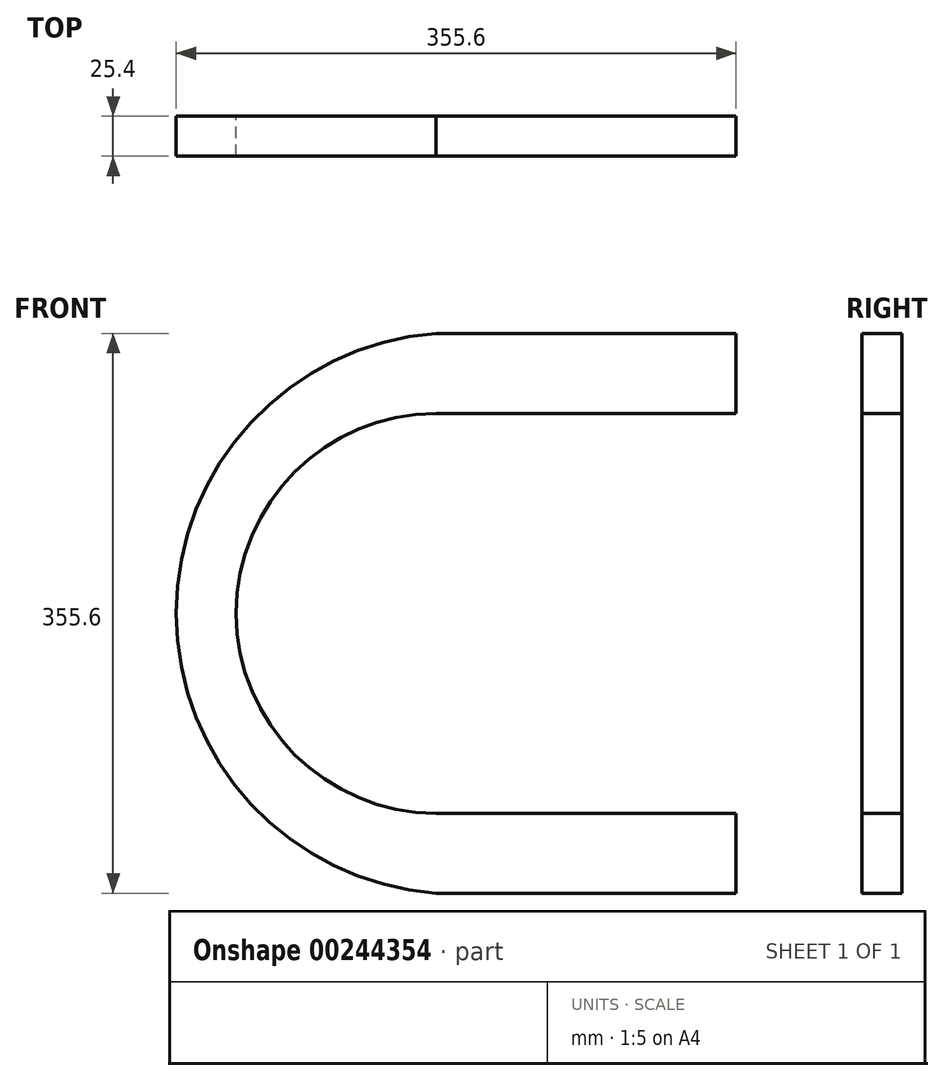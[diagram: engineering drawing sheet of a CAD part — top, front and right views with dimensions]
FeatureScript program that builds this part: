
annotation { "Feature Type Name" : "Feature", "Feature Type Description" : "" }
export const myFeature = defineFeature(function(context is Context, id is Id, definition is map)
    precondition{}
    {
        {
            var Q0;
            Q0=qCreatedBy(makeId("Front.planeOp"),FACE);
            var sketch = newSketch(context, id + "F0", { "sketchPlane" : qUnion([Q0])});
            skLineSegment(sketch, "E0.bottom", {"start": v(190.5, 177.8) * mm, "end": v(-190.5, 177.8) * mm});
            skLineSegment(sketch, "E0.top", {"start": v(190.5, -177.8) * mm, "end": v(-190.5, -177.8) * mm});
            skLineSegment(sketch, "E0.left", {"start": v(190.5, 177.8) * mm, "end": v(190.5, -177.8) * mm});
            skLineSegment(sketch, "E0.right", {"start": v(-190.5, 177.8) * mm, "end": v(-190.5, -177.8) * mm});
            skPoint(sketch, "E0.middle", {"position": v(0, 0) * mm});
            skCircle(sketch, "E1", {"center": v(0, 0) * mm, "radius": 127 * mm});
            skArc(sketch, "E2", {"start": v(0, 177.8) * mm, "mid": v(-165.1, 0) * mm, "end": v(0, -177.8) * mm});
            skLineSegment(sketch, "E3", {"start": v(0, 177.8) * mm, "end": v(318.28, 177.8) * mm});
            skLineSegment(sketch, "E4", {"start": v(0, 127) * mm, "end": v(318.28, 127) * mm});
            skLineSegment(sketch, "E5", {"start": v(0, -127) * mm, "end": v(318.28, -127) * mm});
            skLineSegment(sketch, "E6", {"start": v(0, -177.8) * mm, "end": v(318.28, -177.8) * mm});
            skLineSegment(sketch, "E7.bottom", {"start": v(190.5, 177.8) * mm, "end": v(106.81, 177.8) * mm});
            skLineSegment(sketch, "E7.top", {"start": v(190.5, 261.56) * mm, "end": v(106.81, 261.56) * mm});
            skLineSegment(sketch, "E7.left", {"start": v(190.5, 177.8) * mm, "end": v(190.5, 261.56) * mm});
            skLineSegment(sketch, "E7.right", {"start": v(106.81, 177.8) * mm, "end": v(106.81, 261.56) * mm});
            skLineSegment(sketch, "E8.bottom", {"start": v(190.5, -177.8) * mm, "end": v(106.81, -177.8) * mm});
            skLineSegment(sketch, "E8.top", {"start": v(190.5, -239.72) * mm, "end": v(106.81, -239.72) * mm});
            skLineSegment(sketch, "E8.left", {"start": v(190.5, -177.8) * mm, "end": v(190.5, -239.72) * mm});
            skLineSegment(sketch, "E8.right", {"start": v(106.81, -177.8) * mm, "end": v(106.81, -239.72) * mm});
            skSolve(sketch);
        }
        {
            var Q0;
            {var subQ12=sQuery(id+"F0.wireOp",EDGE,"E2");Q0=makeQuery(id+"F0.imprint","IMPRINT",FACE,{"disambiguationData":[TD([[makeQuery(id+"F0.imprint","IMPRINT",EDGE,{"derivedFrom":subQ12}),1.0]])]});}
            var Q1;
            Q1=makeQuery(id+"F0.imprint","IMPRINT",FACE,{"disambiguationData":[TD([[makeQuery(id+"F0.imprint","IMPRINT",EDGE,{"derivedFrom":sQuery(id+"F0.wireOp",EDGE,"E7.bottom")}),-1.0]])]});
            var Q2;
            Q2=makeQuery(id+"F0.imprint","IMPRINT",FACE,{"disambiguationData":[TD([[makeQuery(id+"F0.imprint","IMPRINT",EDGE,{"derivedFrom":sQuery(id+"F0.wireOp",EDGE,"E8.bottom")}),1.0]])]});
            extrude(context, id + "F1", {"entities" : qUnion([Q0, Q1, Q2]), "depth" : 25.4 * mm});
        }
    });
